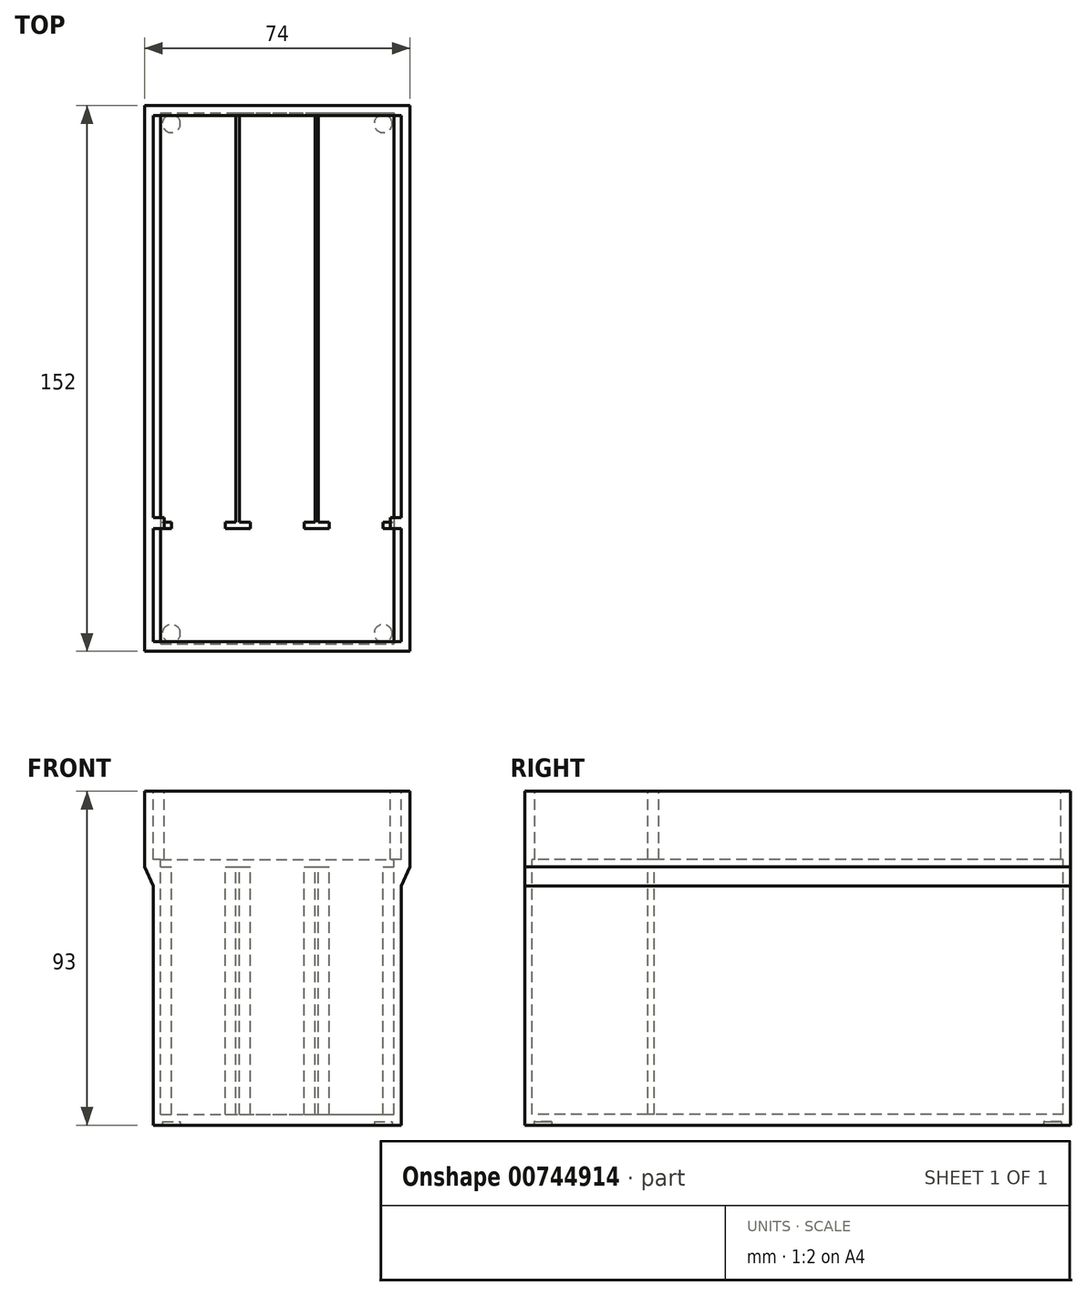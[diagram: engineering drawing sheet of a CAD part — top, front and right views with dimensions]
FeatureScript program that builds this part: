
annotation { "Feature Type Name" : "Feature", "Feature Type Description" : "" }
export const myFeature = defineFeature(function(context is Context, id is Id, definition is map)
    precondition{}
    {
        {
            var Q0;
            Q0=qCreatedBy(makeId("Top.planeOp"),FACE);
            var sketch = newSketch(context, id + "F0", { "sketchPlane" : qUnion([Q0])});
            skLineSegment(sketch, "E0.bottom", {"start": v(34.5, -76) * mm, "end": v(-34.5, -76) * mm});
            skLineSegment(sketch, "E0.top", {"start": v(34.5, 76) * mm, "end": v(-34.5, 76) * mm});
            skLineSegment(sketch, "E0.left", {"start": v(34.5, -76) * mm, "end": v(34.5, 76) * mm});
            skLineSegment(sketch, "E0.right", {"start": v(-34.5, -76) * mm, "end": v(-34.5, 76) * mm});
            skPoint(sketch, "E0.middle", {"position": v(0, 0) * mm});
            skSolve(sketch);
        }
        {
            var Q0;
            Q0 = qSketchRegion(id + "F0", true);
            extrude(context, id + "F1", {"entities" : qUnion([Q0]), "depth" : 72 * mm, "offsetDistance" : 25 * mm});
        }
        {
            var Q0;
            Q0=makeQuery(id+"F1.opExtrude","CAP_FACE",FACE,{"disambiguationData":[OSD([sQuery(id+"F0.wireOp",EDGE,"E0.bottom"),sQuery(id+"F0.wireOp",EDGE,"E0.top"),sQuery(id+"F0.wireOp",EDGE,"E0.left"),sQuery(id+"F0.wireOp",EDGE,"E0.right")])],"isStart":false});
            var sketch = newSketch(context, id + "F2", { "sketchPlane" : qUnion([Q0])});
            skLineSegment(sketch, "E1.bottom", {"start": v(-32.5, 74) * mm, "end": v(-11.5, 74) * mm});
            skLineSegment(sketch, "E1.top", {"start": v(-32.5, -40) * mm, "end": v(-11.5, -40) * mm});
            skLineSegment(sketch, "E1.left", {"start": v(-32.5, 74) * mm, "end": v(-32.5, -40) * mm});
            skLineSegment(sketch, "E1.right", {"start": v(-11.5, 74) * mm, "end": v(-11.5, -40) * mm});
            skLineSegment(sketch, "E2.1.0.0", {"start": v(-10.5, 74) * mm, "end": v(10.5, 74) * mm});
            skLineSegment(sketch, "E2.1.0.1", {"start": v(-10.5, -40) * mm, "end": v(10.5, -40) * mm});
            skLineSegment(sketch, "E2.1.0.2", {"start": v(-10.5, 74) * mm, "end": v(-10.5, -40) * mm});
            skLineSegment(sketch, "E2.1.0.3", {"start": v(10.5, 74) * mm, "end": v(10.5, -40) * mm});
            skLineSegment(sketch, "E2.2.0.0", {"start": v(11.5, 74) * mm, "end": v(32.5, 74) * mm});
            skLineSegment(sketch, "E2.2.0.1", {"start": v(11.5, -40) * mm, "end": v(32.5, -40) * mm});
            skLineSegment(sketch, "E2.2.0.2", {"start": v(11.5, 74) * mm, "end": v(11.5, -40) * mm});
            skLineSegment(sketch, "E2.2.0.3", {"start": v(32.5, 74) * mm, "end": v(32.5, -40) * mm});
            skLineSegment(sketch, "E2.direction1", {"start": v(-32.5, -40) * mm, "end": v(-10.5, -40) * mm, "construction": true});
            skLineSegment(sketch, "E3.bottom", {"start": v(-29.5, -40) * mm, "end": v(-14.5, -40) * mm});
            skLineSegment(sketch, "E3.top", {"start": v(-29.5, -41.75) * mm, "end": v(-14.5, -41.75) * mm});
            skLineSegment(sketch, "E3.left", {"start": v(-29.5, -40) * mm, "end": v(-29.5, -41.75) * mm});
            skLineSegment(sketch, "E3.right", {"start": v(-14.5, -40) * mm, "end": v(-14.5, -41.75) * mm});
            skLineSegment(sketch, "E4.1.0.0", {"start": v(7.5, -40) * mm, "end": v(7.5, -41.75) * mm});
            skLineSegment(sketch, "E4.1.0.1", {"start": v(-7.5, -40) * mm, "end": v(7.5, -40) * mm});
            skLineSegment(sketch, "E4.1.0.2", {"start": v(-7.5, -41.75) * mm, "end": v(7.5, -41.75) * mm});
            skLineSegment(sketch, "E4.1.0.3", {"start": v(-7.5, -40) * mm, "end": v(-7.5, -41.75) * mm});
            skLineSegment(sketch, "E4.2.0.0", {"start": v(29.5, -40) * mm, "end": v(29.5, -41.75) * mm});
            skLineSegment(sketch, "E4.2.0.1", {"start": v(14.5, -40) * mm, "end": v(29.5, -40) * mm});
            skLineSegment(sketch, "E4.2.0.2", {"start": v(14.5, -41.75) * mm, "end": v(29.5, -41.75) * mm});
            skLineSegment(sketch, "E4.2.0.3", {"start": v(14.5, -40) * mm, "end": v(14.5, -41.75) * mm});
            skLineSegment(sketch, "E4.direction1", {"start": v(-29.5, -41.75) * mm, "end": v(-7.5, -41.75) * mm, "construction": true});
            skLineSegment(sketch, "E5.bottom", {"start": v(-32.5, -41.75) * mm, "end": v(32.5, -41.75) * mm});
            skLineSegment(sketch, "E5.top", {"start": v(-32.5, -74) * mm, "end": v(32.5, -74) * mm});
            skLineSegment(sketch, "E5.left", {"start": v(-32.5, -41.75) * mm, "end": v(-32.5, -74) * mm});
            skLineSegment(sketch, "E5.right", {"start": v(32.5, -41.75) * mm, "end": v(32.5, -74) * mm});
            skSolve(sketch);
        }
        {
            var Q0;
            Q0 = qSketchRegion(id + "F2", true);
            extrude(context, id + "F3", {"entities" : qUnion([Q0]), "operationType" : NewBodyOperationType.REMOVE, "oppositeDirection" : true, "depth" : 69 * mm, "offsetDistance" : 25 * mm});
        }
        {
            var Q0;
            Q0=makeQuery(id+"F1.opExtrude","CAP_FACE",FACE,{"disambiguationData":[OSD([sQuery(id+"F0.wireOp",EDGE,"E0.bottom"),sQuery(id+"F0.wireOp",EDGE,"E0.top"),sQuery(id+"F0.wireOp",EDGE,"E0.left"),sQuery(id+"F0.wireOp",EDGE,"E0.right")])],"isStart":false});
            var sketch = newSketch(context, id + "F4", { "sketchPlane" : qUnion([Q0])});
            skLineSegment(sketch, "E6.bottom", {"start": v(37, -76) * mm, "end": v(-37, -76) * mm});
            skLineSegment(sketch, "E6.top", {"start": v(37, 76) * mm, "end": v(-37, 76) * mm});
            skLineSegment(sketch, "E6.left", {"start": v(37, -76) * mm, "end": v(37, 76) * mm});
            skLineSegment(sketch, "E6.right", {"start": v(-37, -76) * mm, "end": v(-37, 76) * mm});
            skPoint(sketch, "E6.middle", {"position": v(0, 0) * mm});
            skSolve(sketch);
        }
        {
            var Q0;
            Q0 = qSketchRegion(id + "F4", true);
            extrude(context, id + "F5", {"entities" : qUnion([Q0]), "operationType" : NewBodyOperationType.ADD, "depth" : 21 * mm, "offsetDistance" : 25 * mm});
        }
        {
            var Q0;
            Q0=makeQuery(id+"F5.opExtrude","CAP_FACE",FACE,{"disambiguationData":[OSD([sQuery(id+"F4.wireOp",EDGE,"E6.bottom"),sQuery(id+"F4.wireOp",EDGE,"E6.top"),sQuery(id+"F4.wireOp",EDGE,"E6.left"),sQuery(id+"F4.wireOp",EDGE,"E6.right")])],"isStart":false});
            var sketch = newSketch(context, id + "F6", { "sketchPlane" : qUnion([Q0])});
            skLineSegment(sketch, "E7.bottom", {"start": v(34.5, -38.75) * mm, "end": v(-34.5, -38.75) * mm});
            skLineSegment(sketch, "E7.top", {"start": v(34.5, 73.25) * mm, "end": v(-34.5, 73.25) * mm});
            skLineSegment(sketch, "E7.left", {"start": v(34.5, -38.75) * mm, "end": v(34.5, 73.25) * mm});
            skLineSegment(sketch, "E7.right", {"start": v(-34.5, -38.75) * mm, "end": v(-34.5, 73.25) * mm});
            skPoint(sketch, "E7.middle", {"position": v(0, 17.25) * mm});
            skLineSegment(sketch, "E8.bottom", {"start": v(-31.5, -38.75) * mm, "end": v(31.5, -38.75) * mm});
            skLineSegment(sketch, "E8.top", {"start": v(-31.5, -41.75) * mm, "end": v(31.5, -41.75) * mm});
            skLineSegment(sketch, "E8.left", {"start": v(-31.5, -38.75) * mm, "end": v(-31.5, -41.75) * mm});
            skLineSegment(sketch, "E8.right", {"start": v(31.5, -38.75) * mm, "end": v(31.5, -41.75) * mm});
            skLineSegment(sketch, "E9.bottom", {"start": v(-34.5, -41.75) * mm, "end": v(34.5, -41.75) * mm});
            skLineSegment(sketch, "E9.top", {"start": v(-34.5, -73.25) * mm, "end": v(34.5, -73.25) * mm});
            skLineSegment(sketch, "E9.left", {"start": v(-34.5, -41.75) * mm, "end": v(-34.5, -73.25) * mm});
            skLineSegment(sketch, "E9.right", {"start": v(34.5, -41.75) * mm, "end": v(34.5, -73.25) * mm});
            skSolve(sketch);
        }
        {
            var Q0;
            Q0 = qSketchRegion(id + "F6", true);
            extrude(context, id + "F7", {"entities" : qUnion([Q0]), "operationType" : NewBodyOperationType.REMOVE, "oppositeDirection" : true, "depth" : 19 * mm, "offsetDistance" : 25 * mm});
        }
        {
            var Q0;
            Q0=makeQuery(id+"F7.boolean.opBoolean","COPY",FACE,{"derivedFrom":makeQuery(id+"F7.opExtrude","CAP_FACE",FACE,{"disambiguationData":[OSD([sQuery(id+"F6.wireOp",EDGE,"E7.bottom"),sQuery(id+"F6.wireOp",EDGE,"E7.top"),sQuery(id+"F6.wireOp",EDGE,"E7.left"),sQuery(id+"F6.wireOp",EDGE,"E7.right"),sQuery(id+"F6.wireOp",EDGE,"E8.left"),sQuery(id+"F6.wireOp",EDGE,"E8.right"),sQuery(id+"F6.wireOp",EDGE,"E9.bottom"),sQuery(id+"F6.wireOp",EDGE,"E9.top"),sQuery(id+"F6.wireOp",EDGE,"E9.left"),sQuery(id+"F6.wireOp",EDGE,"E9.right")])],"isStart":false})});
            var sketch = newSketch(context, id + "F8", { "sketchPlane" : qUnion([Q0])});
            skLineSegment(sketch, "E10.0", {"start": v(-32.5, 74) * mm, "end": v(-32.5, -40) * mm});
            skLineSegment(sketch, "E11.0", {"start": v(32.5, 74) * mm, "end": v(32.5, -40) * mm});
            skLineSegment(sketch, "E12.0", {"start": v(-32.5, -41.75) * mm, "end": v(-32.5, -74) * mm});
            skLineSegment(sketch, "E13.0", {"start": v(32.5, -41.75) * mm, "end": v(32.5, -74) * mm});
            skLineSegment(sketch, "E14.bottom", {"start": v(-32.5, 74) * mm, "end": v(32.5, 74) * mm});
            skLineSegment(sketch, "E14.top", {"start": v(-32.5, -74) * mm, "end": v(32.5, -74) * mm});
            skLineSegment(sketch, "E14.left", {"start": v(-32.5, 74) * mm, "end": v(-32.5, -74) * mm});
            skLineSegment(sketch, "E14.right", {"start": v(32.5, 74) * mm, "end": v(32.5, -74) * mm});
            skSolve(sketch);
        }
        {
            var Q0;
            Q0 = qSketchRegion(id + "F8", true);
            extrude(context, id + "F9", {"entities" : qUnion([Q0]), "operationType" : NewBodyOperationType.REMOVE, "oppositeDirection" : true, "depth" : 2 * mm, "offsetDistance" : 25 * mm});
        }
        {
            var Q0;
            Q0=makeQuery(id+"F5.boolean.opBoolean","MERGE",FACE,{"derivedFrom":[makeQuery(id+"F1.opExtrude","SWEPT_FACE",FACE,{"disambiguationData":[OSD([sQuery(id+"F0.wireOp",EDGE,"E0.bottom")])]}),makeQuery(id+"F5.opExtrude","SWEPT_FACE",FACE,{"disambiguationData":[OSD([sQuery(id+"F4.wireOp",EDGE,"E6.bottom")])]})]});
            var sketch = newSketch(context, id + "F10", { "sketchPlane" : qUnion([Q0])});
            skLineSegment(sketch, "E15", {"start": v(-37, 72) * mm, "end": v(-34.5, 66.64) * mm});
            skLineSegment(sketch, "E16", {"start": v(34.5, 66.64) * mm, "end": v(37, 72) * mm});
            skSolve(sketch);
        }
        {
            var Q0;
            {var subQ0=sQuery(id+"F10.wireOp",EDGE,"E15");Q0=makeQuery(id+"F10.imprint","IMPRINT",FACE,{"disambiguationData":[TD([[makeQuery(id+"F10.imprint","IMPRINT",EDGE,{"derivedFrom":subQ0}),1.0]])]});}
            var Q1;
            {var subQ0=sQuery(id+"F10.wireOp",EDGE,"E16");Q1=makeQuery(id+"F10.imprint","IMPRINT",FACE,{"disambiguationData":[TD([[makeQuery(id+"F10.imprint","IMPRINT",EDGE,{"derivedFrom":subQ0}),1.0]])]});}
            var Q2;
            Q2=makeQuery(id+"F5.boolean.opBoolean","MERGE",FACE,{"derivedFrom":[makeQuery(id+"F1.opExtrude","SWEPT_FACE",FACE,{"disambiguationData":[OSD([sQuery(id+"F0.wireOp",EDGE,"E0.top")])]}),makeQuery(id+"F5.opExtrude","SWEPT_FACE",FACE,{"disambiguationData":[OSD([sQuery(id+"F4.wireOp",EDGE,"E6.top")])]})]});
            extrude(context, id + "F11", {"entities" : qUnion([Q0, Q1]), "operationType" : NewBodyOperationType.ADD, "endBound" : BoundingType.UP_TO_SURFACE, "oppositeDirection" : true, "depth" : 25 * mm, "endBoundEntityFace" : qUnion([Q2]), "offsetDistance" : 25 * mm});
        }
        {
            var Q0;
            Q0=makeQuery(id+"F1.opExtrude","CAP_FACE",FACE,{"disambiguationData":[OSD([sQuery(id+"F0.wireOp",EDGE,"E0.bottom"),sQuery(id+"F0.wireOp",EDGE,"E0.top"),sQuery(id+"F0.wireOp",EDGE,"E0.left"),sQuery(id+"F0.wireOp",EDGE,"E0.right")])],"isStart":true});
            var sketch = newSketch(context, id + "F12", { "sketchPlane" : qUnion([Q0])});
            skLineSegment(sketch, "E17", {"start": v(-65.25, 71) * mm, "end": v(68.42, 71) * mm, "construction": true});
            skLineSegment(sketch, "E18", {"start": v(29.5, 102.08) * mm, "end": v(29.5, -111.73) * mm, "construction": true});
            skLineSegment(sketch, "E19", {"start": v(-29.5, -111.73) * mm, "end": v(-29.5, 118.2) * mm, "construction": true});
            skLineSegment(sketch, "E20", {"start": v(-71.98, -71) * mm, "end": v(80.03, -71) * mm, "construction": true});
            skLineSegment(sketch, "E21.0", {"start": v(-34.5, 76) * mm, "end": v(-34.5, -76) * mm, "construction": true});
            skLineSegment(sketch, "E22.0", {"start": v(34.5, 76) * mm, "end": v(34.5, -76) * mm, "construction": true});
            skCircle(sketch, "E23", {"center": v(-29.5, 71) * mm, "radius": 2.5 * mm});
            skCircle(sketch, "E24", {"center": v(29.5, 71) * mm, "radius": 2.5 * mm});
            skCircle(sketch, "E25", {"center": v(-29.5, -71) * mm, "radius": 2.5 * mm});
            skCircle(sketch, "E26", {"center": v(29.5, -71) * mm, "radius": 2.5 * mm});
            skSolve(sketch);
        }
        {
            var Q0;
            Q0=makeQuery(id+"F12.imprint","IMPRINT",FACE,{"disambiguationData":[TD([[makeQuery(id+"F12.imprint","IMPRINT",EDGE,{"derivedFrom":sQuery(id+"F12.wireOp",EDGE,"E23")}),1.0]])]});
            var Q1;
            Q1=makeQuery(id+"F12.imprint","IMPRINT",FACE,{"disambiguationData":[TD([[makeQuery(id+"F12.imprint","IMPRINT",EDGE,{"derivedFrom":sQuery(id+"F12.wireOp",EDGE,"E24")}),1.0]])]});
            var Q2;
            Q2=makeQuery(id+"F12.imprint","IMPRINT",FACE,{"disambiguationData":[TD([[makeQuery(id+"F12.imprint","IMPRINT",EDGE,{"derivedFrom":sQuery(id+"F12.wireOp",EDGE,"E26")}),1.0]])]});
            var Q3;
            Q3=makeQuery(id+"F12.imprint","IMPRINT",FACE,{"disambiguationData":[TD([[makeQuery(id+"F12.imprint","IMPRINT",EDGE,{"derivedFrom":sQuery(id+"F12.wireOp",EDGE,"E25")}),1.0]])]});
            extrude(context, id + "F13", {"entities" : qUnion([Q0, Q1, Q2, Q3]), "operationType" : NewBodyOperationType.REMOVE, "oppositeDirection" : true, "depth" : 1 * mm, "offsetDistance" : 25 * mm});
        }
    });
